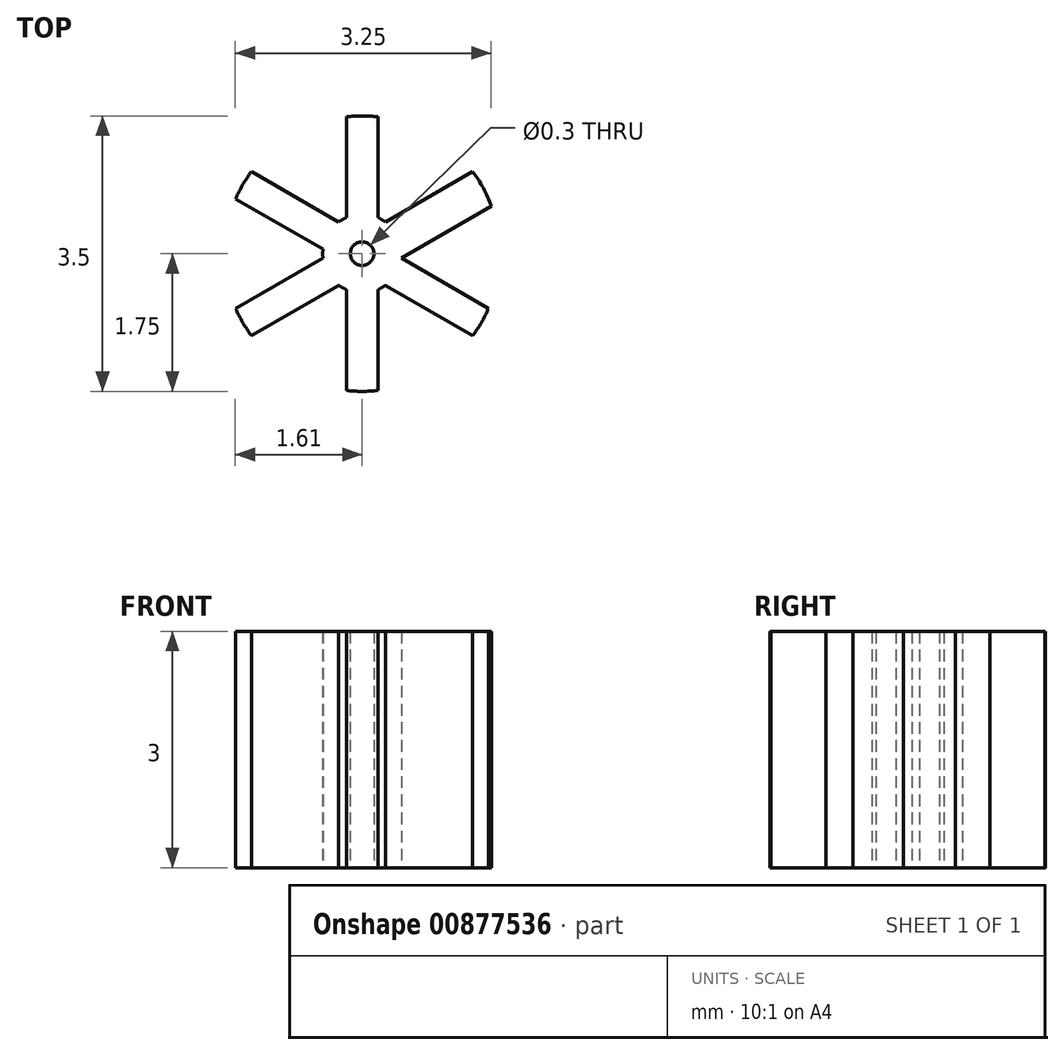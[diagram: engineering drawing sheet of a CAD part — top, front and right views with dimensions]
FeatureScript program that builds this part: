
annotation { "Feature Type Name" : "Feature", "Feature Type Description" : "" }
export const myFeature = defineFeature(function(context is Context, id is Id, definition is map)
    precondition{}
    {
        {
            var Q0;
            Q0=qCreatedBy(makeId("Top.planeOp"),FACE);
            var sketch = newSketch(context, id + "F0", { "sketchPlane" : qUnion([Q0])});
            skArc(sketch, "E0", {"start": v(0.2, 1.74) * mm, "mid": v(0, 1.75) * mm, "end": v(-0.2, 1.74) * mm});
            skLineSegment(sketch, "E1.3.0", {"start": v(0.2, -0.46) * mm, "end": v(0.2, -1.74) * mm});
            skLineSegment(sketch, "E1.3.1", {"start": v(-0.2, -0.46) * mm, "end": v(-0.2, -1.74) * mm});
            skLineSegment(sketch, "E1.4.0", {"start": v(0.5, -0.06) * mm, "end": v(1.6, -0.7) * mm});
            skLineSegment(sketch, "E1.4.1", {"start": v(0.3, -0.4) * mm, "end": v(1.4, -1.04) * mm});
            skLineSegment(sketch, "E1.5.1", {"start": v(0.5, -0.06) * mm, "end": v(1.64, 0.6) * mm});
            skArc(sketch, "E2", {"start": v(0.2, -0.46) * mm, "mid": v(0.25, -0.43) * mm, "end": v(0.3, -0.4) * mm});
            skArc(sketch, "E3.trimOffspring", {"start": v(-1.4, 1.04) * mm, "mid": v(-1.52, 0.87) * mm, "end": v(-1.6, 0.7) * mm});
            skArc(sketch, "E4.trimOffspring", {"start": v(-1.6, -0.7) * mm, "mid": v(-1.52, -0.87) * mm, "end": v(-1.4, -1.04) * mm});
            skArc(sketch, "E5.trimOffspring", {"start": v(-0.2, -1.74) * mm, "mid": v(0, -1.75) * mm, "end": v(0.2, -1.74) * mm});
            skArc(sketch, "E6.trimOffspring", {"start": v(1.4, -1.04) * mm, "mid": v(1.52, -0.88) * mm, "end": v(1.6, -0.7) * mm});
            skArc(sketch, "E7.trimOffspring", {"start": v(1.64, 0.6) * mm, "mid": v(1.54, 0.83) * mm, "end": v(1.4, 1.04) * mm});
            skLineSegment(sketch, "E8.trimOffspring", {"start": v(-0.2, 0.46) * mm, "end": v(-0.2, 1.74) * mm});
            skLineSegment(sketch, "E9.trimOffspring", {"start": v(0.2, 0.46) * mm, "end": v(0.2, 1.74) * mm});
            skLineSegment(sketch, "E10.trimOffspring", {"start": v(0.3, 0.4) * mm, "end": v(1.4, 1.04) * mm});
            skLineSegment(sketch, "E11.trimOffspring", {"start": v(-0.3, 0.4) * mm, "end": v(-1.4, 1.04) * mm});
            skLineSegment(sketch, "E12.trimOffspring", {"start": v(-0.5, -0.06) * mm, "end": v(-1.6, -0.7) * mm});
            skLineSegment(sketch, "E13.trimOffspring", {"start": v(-0.5, 0.06) * mm, "end": v(-1.6, 0.7) * mm});
            skLineSegment(sketch, "E14.trimOffspring", {"start": v(-0.3, -0.4) * mm, "end": v(-1.4, -1.04) * mm});
            skArc(sketch, "E15.trimOffspring", {"start": v(-0.3, -0.4) * mm, "mid": v(-0.25, -0.43) * mm, "end": v(-0.2, -0.46) * mm});
            skArc(sketch, "E16.trimOffspring", {"start": v(-0.5, 0.06) * mm, "mid": v(-0.5, 0) * mm, "end": v(-0.5, -0.06) * mm});
            skArc(sketch, "E17.trimOffspring", {"start": v(-0.2, 0.46) * mm, "mid": v(-0.25, 0.43) * mm, "end": v(-0.3, 0.4) * mm});
            skArc(sketch, "E18.trimOffspring", {"start": v(0.3, 0.4) * mm, "mid": v(0.25, 0.43) * mm, "end": v(0.2, 0.46) * mm});
            skSolve(sketch);
        }
        {
            var Q0;
            Q0 = qSketchRegion(id + "F0", true);
            extrude(context, id + "F1", {"entities" : qUnion([Q0]), "depth" : 3 * mm, "offsetDistance" : 25 * mm});
        }
        {
            var Q0;
            Q0=qCreatedBy(makeId("Top.planeOp"),FACE);
            var sketch = newSketch(context, id + "F2", { "sketchPlane" : qUnion([Q0])});
            skCircle(sketch, "E19", {"center": v(0, 0) * mm, "radius": 0.15 * mm});
            skSolve(sketch);
        }
        {
            var Q0;
            Q0 = qSketchRegion(id + "F2", true);
            extrude(context, id + "F3", {"entities" : qUnion([Q0]), "operationType" : NewBodyOperationType.REMOVE, "depth" : 5 * mm, "offsetDistance" : 25 * mm});
        }
    });
